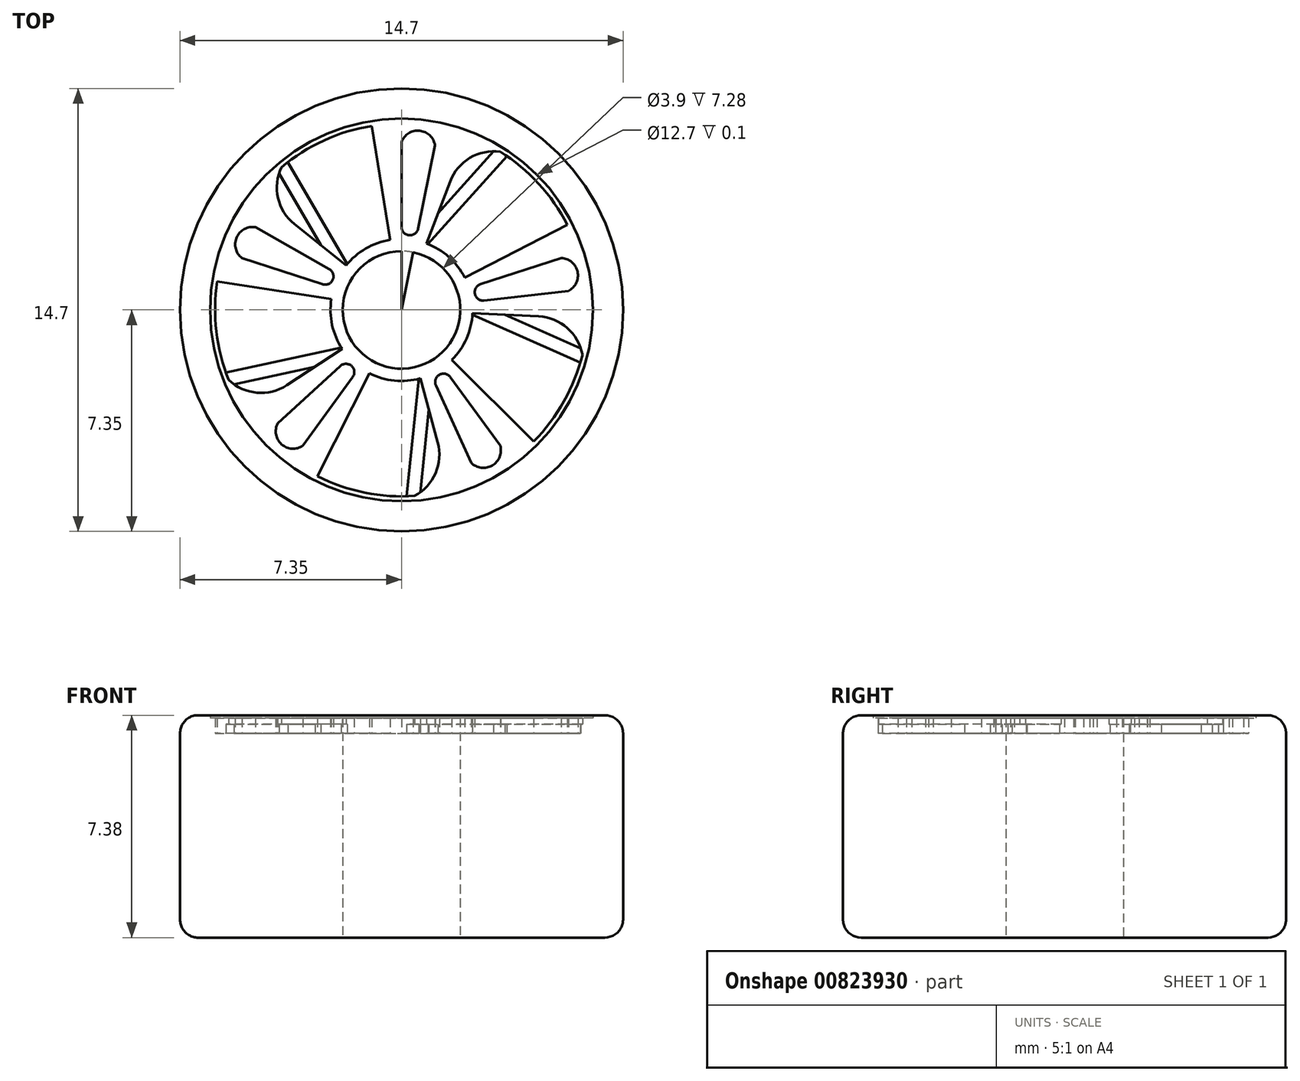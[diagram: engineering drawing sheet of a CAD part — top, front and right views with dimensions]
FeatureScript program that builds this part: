
annotation { "Feature Type Name" : "Feature", "Feature Type Description" : "" }
export const myFeature = defineFeature(function(context is Context, id is Id, definition is map)
    precondition{}
    {
        {
            var Q0;
            Q0=qCreatedBy(makeId("Front.planeOp"),FACE);
            var sketch = newSketch(context, id + "F0", { "sketchPlane" : qUnion([Q0])});
            skLineSegment(sketch, "E0.bottom", {"start": v(0, 0) * mm, "end": v(7.35, 0) * mm});
            skLineSegment(sketch, "E0.top", {"start": v(0, 7.38) * mm, "end": v(7.35, 7.38) * mm});
            skLineSegment(sketch, "E0.left", {"start": v(0, 0) * mm, "end": v(0, 7.38) * mm});
            skLineSegment(sketch, "E0.right", {"start": v(7.35, 0) * mm, "end": v(7.35, 7.38) * mm});
            skLineSegment(sketch, "E1.bottom", {"start": v(0, 7.38) * mm, "end": v(1.95, 7.38) * mm});
            skLineSegment(sketch, "E1.top", {"start": v(0, 0) * mm, "end": v(1.95, 0) * mm});
            skLineSegment(sketch, "E1.left", {"start": v(0, 7.38) * mm, "end": v(0, 0) * mm});
            skLineSegment(sketch, "E1.right", {"start": v(1.95, 7.38) * mm, "end": v(1.95, 0) * mm});
            skLineSegment(sketch, "E2.bottom", {"start": v(0, 7.38) * mm, "end": v(6.75, 7.38) * mm});
            skLineSegment(sketch, "E2.top", {"start": v(0, 0) * mm, "end": v(6.75, 0) * mm});
            skLineSegment(sketch, "E2.right", {"start": v(6.75, 7.38) * mm, "end": v(6.75, 0) * mm});
            skLineSegment(sketch, "E3.top", {"start": v(0, 6.78) * mm, "end": v(7.35, 6.78) * mm});
            skLineSegment(sketch, "E3.left", {"start": v(0, 0) * mm, "end": v(0, 6.78) * mm});
            skLineSegment(sketch, "E3.right", {"start": v(7.35, 0) * mm, "end": v(7.35, 6.78) * mm});
            skLineSegment(sketch, "E4.top", {"start": v(0, 0.6) * mm, "end": v(7.35, 0.6) * mm});
            skLineSegment(sketch, "E4.left", {"start": v(0, 7.38) * mm, "end": v(0, 0.6) * mm});
            skLineSegment(sketch, "E4.right", {"start": v(7.35, 7.38) * mm, "end": v(7.35, 0.6) * mm});
            skLineSegment(sketch, "E5.bottom", {"start": v(0, 7.38) * mm, "end": v(6.35, 7.38) * mm});
            skLineSegment(sketch, "E5.top", {"start": v(0, 0) * mm, "end": v(6.35, 0) * mm});
            skLineSegment(sketch, "E5.right", {"start": v(6.35, 7.38) * mm, "end": v(6.35, 0) * mm});
            skArc(sketch, "E6", {"start": v(7.35, 6.78) * mm, "mid": v(7.17, 7.2) * mm, "end": v(6.75, 7.38) * mm});
            skArc(sketch, "E7", {"start": v(6.75, 0) * mm, "mid": v(7.17, 0.18) * mm, "end": v(7.35, 0.6) * mm});
            skSolve(sketch);
        }
        {
            var Q0;
            {var subQ0=sQuery(id+"F0.wireOp",EDGE,"E3.top");var subQ1=sQuery(id+"F0.wireOp",EDGE,"E1.right");var subQ2=makeQuery(id+"F0.imprint","INTERSECT",VERTEX,{"derivedFrom":[subQ1,subQ0]});Q0=makeQuery(id+"F0.imprint","IMPRINT",FACE,{"disambiguationData":[TD([[makeQuery(id+"F0.imprint","IMPRINT",EDGE,{"disambiguationData":[TD([[subQ2,-1.0]])],"derivedFrom":subQ1}),1.0]])]});}
            var Q1;
            {var subQ0=sQuery(id+"F0.wireOp",EDGE,"E3.top");var subQ1=sQuery(id+"F0.wireOp",EDGE,"E2.right");var subQ2=makeQuery(id+"F0.imprint","INTERSECT",VERTEX,{"derivedFrom":[subQ1,subQ0]});Q1=makeQuery(id+"F0.imprint","IMPRINT",FACE,{"disambiguationData":[TD([[makeQuery(id+"F0.imprint","IMPRINT",EDGE,{"disambiguationData":[TD([[subQ2,-1.0]])],"derivedFrom":subQ1}),-1.0]])]});}
            var Q2;
            {var subQ0=sQuery(id+"F0.wireOp",EDGE,"E2.right");var subQ5=sQuery(id+"F0.wireOp",EDGE,"E3.top");var subQ6=makeQuery(id+"F0.imprint","INTERSECT",VERTEX,{"derivedFrom":[subQ0,subQ5]});Q2=makeQuery(id+"F0.imprint","IMPRINT",FACE,{"disambiguationData":[TD([[makeQuery(id+"F0.imprint","IMPRINT",EDGE,{"disambiguationData":[TD([[subQ6,1.0]])],"derivedFrom":subQ5}),1.0]])]});}
            var Q3;
            {var subQ0=sQuery(id+"F0.wireOp",EDGE,"E6");Q3=makeQuery(id+"F0.imprint","IMPRINT",FACE,{"disambiguationData":[TD([[makeQuery(id+"F0.imprint","IMPRINT",EDGE,{"derivedFrom":subQ0}),1.0]])]});}
            var Q4;
            {var subQ3=sQuery(id+"F0.wireOp",EDGE,"E3.top");var subQ5=sQuery(id+"F0.wireOp",EDGE,"E2.right");var subQ7=makeQuery(id+"F0.imprint","INTERSECT",VERTEX,{"derivedFrom":[subQ5,subQ3]});Q4=makeQuery(id+"F0.imprint","IMPRINT",FACE,{"disambiguationData":[TD([[makeQuery(id+"F0.imprint","IMPRINT",EDGE,{"disambiguationData":[TD([[subQ7,-1.0]])],"derivedFrom":subQ5}),1.0]])]});}
            var Q5;
            {var subQ0=sQuery(id+"F0.wireOp",EDGE,"E7");Q5=makeQuery(id+"F0.imprint","IMPRINT",FACE,{"disambiguationData":[TD([[makeQuery(id+"F0.imprint","IMPRINT",EDGE,{"derivedFrom":subQ0}),1.0]])]});}
            var Q6;
            {var subQ0=sQuery(id+"F0.wireOp",EDGE,"E2.right");var subQ5=sQuery(id+"F0.wireOp",EDGE,"E4.top");var subQ6=makeQuery(id+"F0.imprint","INTERSECT",VERTEX,{"derivedFrom":[subQ0,subQ5]});Q6=makeQuery(id+"F0.imprint","IMPRINT",FACE,{"disambiguationData":[TD([[makeQuery(id+"F0.imprint","IMPRINT",EDGE,{"disambiguationData":[TD([[subQ6,1.0]])],"derivedFrom":subQ5}),-1.0]])]});}
            var Q7;
            {var subQ0=sQuery(id+"F0.wireOp",EDGE,"E1.right");var subQ1=sQuery(id+"F0.wireOp",EDGE,"E0.bottom");var subQ2=makeQuery(id+"F0.imprint","INTERSECT",VERTEX,{"derivedFrom":[subQ1,subQ0]});Q7=makeQuery(id+"F0.imprint","IMPRINT",FACE,{"disambiguationData":[TD([[makeQuery(id+"F0.imprint","IMPRINT",EDGE,{"disambiguationData":[TD([[subQ2,-1.0]])],"derivedFrom":subQ1}),1.0]])]});}
            var Q8;
            Q8=sQuery(id+"F0.wireOp",EDGE,"E3.left");
            revolve(context, id + "F1", {"surfaceOperationType" : NewSurfaceOperationType.NEW, "entities" : qUnion([Q0, Q1, Q2, Q3, Q4, Q5, Q6, Q7]), "axis" : qUnion([Q8]), "revolveType" : RevolveType.FULL});
        }
        {
            var Q0;
            Q0=makeQuery(id+"F1.opRevolve","SWEPT_FACE",FACE,{"disambiguationData":[OSD([sQuery(id+"F0.wireOp",EDGE,"E3.top")])]});
            var sketch = newSketch(context, id + "F2", { "sketchPlane" : qUnion([Q0])});
            skLineSegment(sketch, "E8", {"start": v(0, 0) * mm, "end": v(2.25, 5.94) * mm});
            skArc(sketch, "E9", {"start": v(4.22, 4.75) * mm, "mid": v(2.78, 5.24) * mm, "end": v(1.61, 4.26) * mm});
            skLineSegment(sketch, "E10", {"start": v(0.79, 2.08) * mm, "end": v(3.56, 5.18) * mm});
            skLineSegment(sketch, "E11", {"start": v(3.05, 5.26) * mm, "end": v(1.21, 3.21) * mm});
            skCircle(sketch, "E12", {"center": v(0, 0) * mm, "radius": 2.36 * mm});
            skLineSegment(sketch, "E13", {"start": v(0, 0) * mm, "end": v(-1.02, 6.27) * mm});
            skLineSegment(sketch, "E14", {"start": v(0, 6.35) * mm, "end": v(0, 0) * mm});
            skLineSegment(sketch, "E15", {"start": v(1.27, 6.22) * mm, "end": v(0, 0) * mm});
            skCircle(sketch, "E16", {"center": v(0, 0) * mm, "radius": 6.19 * mm});
            skLineSegment(sketch, "E17", {"start": v(-0.99, 6.1) * mm, "end": v(2.19, 5.79) * mm});
            skLineSegment(sketch, "E18", {"start": v(0, 5.57) * mm, "end": v(1.11, 5.46) * mm});
            skLineSegment(sketch, "E19", {"start": v(-0.99, 6.1) * mm, "end": v(0.6, 5.95) * mm});
            skArc(sketch, "E20", {"start": v(1.11, 5.46) * mm, "mid": v(0.6, 5.95) * mm, "end": v(0, 5.57) * mm});
            skLineSegment(sketch, "E21", {"start": v(0, 2.75) * mm, "end": v(0.55, 2.7) * mm});
            skArc(sketch, "E22", {"start": v(0, 2.75) * mm, "mid": v(0.25, 2.48) * mm, "end": v(0.55, 2.7) * mm});
            skLineSegment(sketch, "E23.1.0", {"start": v(0, 0) * mm, "end": v(-6.28, 0.97) * mm});
            skLineSegment(sketch, "E23.1.1", {"start": v(-6.04, 1.96) * mm, "end": v(0, 0) * mm});
            skArc(sketch, "E23.1.2", {"start": v(-2.62, 0.85) * mm, "mid": v(-2.28, 1) * mm, "end": v(-2.4, 1.36) * mm});
            skArc(sketch, "E23.1.3", {"start": v(-4.85, 2.74) * mm, "mid": v(-5.47, 2.4) * mm, "end": v(-5.3, 1.72) * mm});
            skLineSegment(sketch, "E23.1.4", {"start": v(-5.53, 3.13) * mm, "end": v(0, 0) * mm});
            skLineSegment(sketch, "E23.1.5", {"start": v(0, 0) * mm, "end": v(-4.96, 3.97) * mm});
            skLineSegment(sketch, "E23.1.6", {"start": v(-1.73, 1.39) * mm, "end": v(-3.83, 4.99) * mm});
            skLineSegment(sketch, "E23.1.7", {"start": v(-4.06, 4.53) * mm, "end": v(-2.68, 2.15) * mm});
            skArc(sketch, "E23.1.8", {"start": v(-3.2, 5.48) * mm, "mid": v(-4.12, 4.26) * mm, "end": v(-3.55, 2.85) * mm});
            skLineSegment(sketch, "E23.2.0", {"start": v(0, 0) * mm, "end": v(-2.86, -5.67) * mm});
            skLineSegment(sketch, "E23.2.1", {"start": v(-3.73, -5.14) * mm, "end": v(0, 0) * mm});
            skArc(sketch, "E23.2.2", {"start": v(-1.62, -2.23) * mm, "mid": v(-1.66, -1.86) * mm, "end": v(-2.03, -1.86) * mm});
            skArc(sketch, "E23.2.3", {"start": v(-4.1, -3.76) * mm, "mid": v(-3.98, -4.46) * mm, "end": v(-3.27, -4.5) * mm});
            skLineSegment(sketch, "E23.2.4", {"start": v(-4.68, -4.29) * mm, "end": v(0, 0) * mm});
            skLineSegment(sketch, "E23.2.5", {"start": v(0, 0) * mm, "end": v(-5.3, -3.49) * mm});
            skLineSegment(sketch, "E23.2.6", {"start": v(-1.86, -1.22) * mm, "end": v(-5.93, -2.1) * mm});
            skLineSegment(sketch, "E23.2.7", {"start": v(-5.56, -2.47) * mm, "end": v(-2.87, -1.89) * mm});
            skArc(sketch, "E23.2.8", {"start": v(-6.2, -1.36) * mm, "mid": v(-5.33, -2.6) * mm, "end": v(-3.8, -2.5) * mm});
            skLineSegment(sketch, "E24.2.3.0", {"start": v(0, 0) * mm, "end": v(4.5, -4.47) * mm});
            skLineSegment(sketch, "E24.3.3.0", {"start": v(3.73, -5.14) * mm, "end": v(0, 0) * mm});
            skArc(sketch, "E24.6.3.0", {"start": v(1.62, -2.23) * mm, "mid": v(1.25, -2.15) * mm, "end": v(1.14, -2.5) * mm});
            skArc(sketch, "E24.10.3.0", {"start": v(2.31, -5.07) * mm, "mid": v(3.01, -5.16) * mm, "end": v(3.27, -4.5) * mm});
            skLineSegment(sketch, "E24.14.3.0", {"start": v(2.63, -5.78) * mm, "end": v(0, 0) * mm});
            skLineSegment(sketch, "E24.17.3.0", {"start": v(0, 0) * mm, "end": v(1.67, -6.13) * mm});
            skLineSegment(sketch, "E24.20.3.0", {"start": v(0.59, -2.14) * mm, "end": v(0.16, -6.29) * mm});
            skLineSegment(sketch, "E24.23.3.0", {"start": v(0.63, -6.05) * mm, "end": v(0.9, -3.31) * mm});
            skArc(sketch, "E24.26.3.0", {"start": v(-0.62, -6.32) * mm, "mid": v(0.83, -5.87) * mm, "end": v(1.2, -4.4) * mm});
            skLineSegment(sketch, "E24.2.4.0", {"start": v(0, 0) * mm, "end": v(5.65, 2.9) * mm});
            skLineSegment(sketch, "E24.3.4.0", {"start": v(6.04, 1.96) * mm, "end": v(0, 0) * mm});
            skArc(sketch, "E24.6.4.0", {"start": v(2.62, 0.85) * mm, "mid": v(2.43, 0.53) * mm, "end": v(2.74, 0.31) * mm});
            skArc(sketch, "E24.10.4.0", {"start": v(5.54, 0.63) * mm, "mid": v(5.84, 1.27) * mm, "end": v(5.3, 1.72) * mm});
            skLineSegment(sketch, "E24.14.4.0", {"start": v(6.3, 0.72) * mm, "end": v(0, 0) * mm});
            skLineSegment(sketch, "E24.17.4.0", {"start": v(0, 0) * mm, "end": v(6.34, -0.3) * mm});
            skLineSegment(sketch, "E24.20.4.0", {"start": v(2.22, -0.1) * mm, "end": v(6.03, -1.79) * mm});
            skLineSegment(sketch, "E24.23.4.0", {"start": v(5.95, -1.27) * mm, "end": v(3.43, -0.16) * mm});
            skArc(sketch, "E24.26.4.0", {"start": v(5.82, -2.55) * mm, "mid": v(5.84, -1.02) * mm, "end": v(4.55, -0.22) * mm});
            skSolve(sketch);
        }
        {
            var Q0;
            {var subQ0=sQuery(id+"F2.wireOp",EDGE,"E23.1.1");var subQ5=sQuery(id+"F2.wireOp",EDGE,"E12");var subQ9=makeQuery(id+"F2.imprint","INTERSECT",VERTEX,{"derivedFrom":[subQ5,subQ0]});Q0=makeQuery(id+"F2.imprint","IMPRINT",FACE,{"disambiguationData":[TD([[makeQuery(id+"F2.imprint","IMPRINT",EDGE,{"disambiguationData":[TD([[subQ9,-1.0]])],"derivedFrom":subQ5}),-1.0]])]});}
            var Q1;
            {var subQ5=sQuery(id+"F2.wireOp",EDGE,"E23.1.2");Q1=makeQuery(id+"F2.imprint","IMPRINT",FACE,{"disambiguationData":[TD([[makeQuery(id+"F2.imprint","IMPRINT",EDGE,{"derivedFrom":subQ5}),-1.0]])]});}
            var Q2;
            {var subQ5=sQuery(id+"F2.wireOp",EDGE,"E23.1.5");var subQ7=sQuery(id+"F2.wireOp",EDGE,"E12");var subQ8=makeQuery(id+"F2.imprint","INTERSECT",VERTEX,{"derivedFrom":[subQ7,subQ5]});Q2=makeQuery(id+"F2.imprint","IMPRINT",FACE,{"disambiguationData":[TD([[makeQuery(id+"F2.imprint","IMPRINT",EDGE,{"disambiguationData":[TD([[subQ8,-1.0]])],"derivedFrom":subQ7}),-1.0]])]});}
            var Q3;
            {var subQ0=sQuery(id+"F2.wireOp",EDGE,"E23.1.8");var subQ1=sQuery(id+"F2.wireOp",EDGE,"E16");var subQ2=makeQuery(id+"F2.imprint","INTERSECT",VERTEX,{"derivedFrom":[subQ1,subQ0]});Q3=makeQuery(id+"F2.imprint","IMPRINT",FACE,{"disambiguationData":[TD([[makeQuery(id+"F2.imprint","IMPRINT",EDGE,{"disambiguationData":[TD([[subQ2,-1.0]])],"derivedFrom":subQ1}),1.0]])]});}
            var Q4;
            {var subQ5=sQuery(id+"F2.wireOp",EDGE,"E22");Q4=makeQuery(id+"F2.imprint","IMPRINT",FACE,{"disambiguationData":[TD([[makeQuery(id+"F2.imprint","IMPRINT",EDGE,{"derivedFrom":subQ5}),-1.0]])]});}
            var Q5;
            {var subQ1=sQuery(id+"F2.wireOp",EDGE,"E8");var subQ8=makeQuery(id+"F2.imprint","INTERSECT",VERTEX,{"derivedFrom":[subQ1,sQuery(id+"F2.wireOp",EDGE,"E11")]});Q5=makeQuery(id+"F2.imprint","IMPRINT",FACE,{"disambiguationData":[TD([[makeQuery(id+"F2.imprint","IMPRINT",EDGE,{"disambiguationData":[TD([[subQ8,1.0]])],"derivedFrom":subQ1}),1.0]])]});}
            var Q6;
            {var subQ0=sQuery(id+"F2.wireOp",EDGE,"E14");var subQ7=sQuery(id+"F2.wireOp",EDGE,"E12");var subQ9=makeQuery(id+"F2.imprint","INTERSECT",VERTEX,{"derivedFrom":[subQ7,subQ0]});Q6=makeQuery(id+"F2.imprint","IMPRINT",FACE,{"disambiguationData":[TD([[makeQuery(id+"F2.imprint","IMPRINT",EDGE,{"disambiguationData":[TD([[subQ9,-1.0]])],"derivedFrom":subQ7}),-1.0]])]});}
            var Q7;
            {var subQ1=sQuery(id+"F2.wireOp",EDGE,"E14");var subQ3=sQuery(id+"F2.wireOp",EDGE,"E19");var subQ4=makeQuery(id+"F2.imprint","INTERSECT",VERTEX,{"derivedFrom":[subQ1,subQ3]});Q7=makeQuery(id+"F2.imprint","IMPRINT",FACE,{"disambiguationData":[TD([[makeQuery(id+"F2.imprint","IMPRINT",EDGE,{"disambiguationData":[TD([[subQ4,-1.0]])],"derivedFrom":subQ1}),1.0]])]});}
            var Q8;
            {var subQ5=sQuery(id+"F2.wireOp",EDGE,"E16");var subQ6=sQuery(id+"F2.wireOp",EDGE,"E14");var subQ7=makeQuery(id+"F2.imprint","INTERSECT",VERTEX,{"derivedFrom":[subQ6,subQ5]});Q8=makeQuery(id+"F2.imprint","IMPRINT",FACE,{"disambiguationData":[TD([[makeQuery(id+"F2.imprint","IMPRINT",EDGE,{"disambiguationData":[TD([[subQ7,-1.0]])],"derivedFrom":subQ6}),1.0]])]});}
            var Q9;
            {var subQ0=sQuery(id+"F2.wireOp",EDGE,"E16");var subQ1=sQuery(id+"F2.wireOp",EDGE,"E14");var subQ2=makeQuery(id+"F2.imprint","INTERSECT",VERTEX,{"derivedFrom":[subQ1,subQ0]});Q9=makeQuery(id+"F2.imprint","IMPRINT",FACE,{"disambiguationData":[TD([[makeQuery(id+"F2.imprint","IMPRINT",EDGE,{"disambiguationData":[TD([[subQ2,-1.0]])],"derivedFrom":subQ1}),-1.0]])]});}
            var Q10;
            {var subQ0=sQuery(id+"F2.wireOp",EDGE,"E16");var subQ1=sQuery(id+"F2.wireOp",EDGE,"E15");var subQ2=makeQuery(id+"F2.imprint","INTERSECT",VERTEX,{"derivedFrom":[subQ1,subQ0]});Q10=makeQuery(id+"F2.imprint","IMPRINT",FACE,{"disambiguationData":[TD([[makeQuery(id+"F2.imprint","IMPRINT",EDGE,{"disambiguationData":[TD([[subQ2,-1.0]])],"derivedFrom":subQ1}),1.0]])]});}
            var Q11;
            {var subQ1=sQuery(id+"F2.wireOp",EDGE,"E15");var subQ3=sQuery(id+"F2.wireOp",EDGE,"E17");var subQ4=makeQuery(id+"F2.imprint","INTERSECT",VERTEX,{"derivedFrom":[subQ1,subQ3]});Q11=makeQuery(id+"F2.imprint","IMPRINT",FACE,{"disambiguationData":[TD([[makeQuery(id+"F2.imprint","IMPRINT",EDGE,{"disambiguationData":[TD([[subQ4,-1.0]])],"derivedFrom":subQ1}),-1.0]])]});}
            var Q12;
            {var subQ0=sQuery(id+"F2.wireOp",EDGE,"E9");var subQ5=makeQuery(id+"F2.imprint","INTERSECT",VERTEX,{"derivedFrom":[subQ0,sQuery(id+"F2.wireOp",EDGE,"E11")]});Q12=makeQuery(id+"F2.imprint","IMPRINT",FACE,{"disambiguationData":[TD([[makeQuery(id+"F2.imprint","IMPRINT",EDGE,{"disambiguationData":[TD([[subQ5,1.0]])],"derivedFrom":subQ0}),-1.0]])]});}
            var Q13;
            {var subQ5=sQuery(id+"F2.wireOp",EDGE,"E24.10.4.0");Q13=makeQuery(id+"F2.imprint","IMPRINT",FACE,{"disambiguationData":[TD([[makeQuery(id+"F2.imprint","IMPRINT",EDGE,{"derivedFrom":subQ5}),-1.0]])]});}
            var Q14;
            {var subQ0=sQuery(id+"F2.wireOp",EDGE,"E24.14.4.0");var subQ7=sQuery(id+"F2.wireOp",EDGE,"E12");var subQ8=makeQuery(id+"F2.imprint","INTERSECT",VERTEX,{"derivedFrom":[subQ7,subQ0]});Q14=makeQuery(id+"F2.imprint","IMPRINT",FACE,{"disambiguationData":[TD([[makeQuery(id+"F2.imprint","IMPRINT",EDGE,{"disambiguationData":[TD([[subQ8,1.0]])],"derivedFrom":subQ7}),-1.0]])]});}
            var Q15;
            {var subQ0=sQuery(id+"F2.wireOp",EDGE,"E24.26.4.0");var subQ1=sQuery(id+"F2.wireOp",EDGE,"E16");var subQ2=makeQuery(id+"F2.imprint","INTERSECT",VERTEX,{"derivedFrom":[subQ1,subQ0]});Q15=makeQuery(id+"F2.imprint","IMPRINT",FACE,{"disambiguationData":[TD([[makeQuery(id+"F2.imprint","IMPRINT",EDGE,{"disambiguationData":[TD([[subQ2,-1.0]])],"derivedFrom":subQ1}),1.0]])]});}
            var Q16;
            {var subQ0=sQuery(id+"F2.wireOp",EDGE,"E24.3.3.0");var subQ5=sQuery(id+"F2.wireOp",EDGE,"E12");var subQ9=makeQuery(id+"F2.imprint","INTERSECT",VERTEX,{"derivedFrom":[subQ5,subQ0]});Q16=makeQuery(id+"F2.imprint","IMPRINT",FACE,{"disambiguationData":[TD([[makeQuery(id+"F2.imprint","IMPRINT",EDGE,{"disambiguationData":[TD([[subQ9,-1.0]])],"derivedFrom":subQ5}),-1.0]])]});}
            var Q17;
            {var subQ5=sQuery(id+"F2.wireOp",EDGE,"E24.10.3.0");Q17=makeQuery(id+"F2.imprint","IMPRINT",FACE,{"disambiguationData":[TD([[makeQuery(id+"F2.imprint","IMPRINT",EDGE,{"derivedFrom":subQ5}),-1.0]])]});}
            var Q18;
            {var subQ5=sQuery(id+"F2.wireOp",EDGE,"E24.6.4.0");Q18=makeQuery(id+"F2.imprint","IMPRINT",FACE,{"disambiguationData":[TD([[makeQuery(id+"F2.imprint","IMPRINT",EDGE,{"derivedFrom":subQ5}),-1.0]])]});}
            var Q19;
            {var subQ5=sQuery(id+"F2.wireOp",EDGE,"E24.6.3.0");Q19=makeQuery(id+"F2.imprint","IMPRINT",FACE,{"disambiguationData":[TD([[makeQuery(id+"F2.imprint","IMPRINT",EDGE,{"derivedFrom":subQ5}),-1.0]])]});}
            var Q20;
            {var subQ4=sQuery(id+"F2.wireOp",EDGE,"E24.17.3.0");var subQ7=sQuery(id+"F2.wireOp",EDGE,"E12");var subQ9=makeQuery(id+"F2.imprint","INTERSECT",VERTEX,{"derivedFrom":[subQ7,subQ4]});Q20=makeQuery(id+"F2.imprint","IMPRINT",FACE,{"disambiguationData":[TD([[makeQuery(id+"F2.imprint","IMPRINT",EDGE,{"disambiguationData":[TD([[subQ9,-1.0]])],"derivedFrom":subQ7}),-1.0]])]});}
            var Q21;
            {var subQ0=sQuery(id+"F2.wireOp",EDGE,"E24.26.3.0");var subQ1=sQuery(id+"F2.wireOp",EDGE,"E16");var subQ2=makeQuery(id+"F2.imprint","INTERSECT",VERTEX,{"derivedFrom":[subQ1,subQ0]});Q21=makeQuery(id+"F2.imprint","IMPRINT",FACE,{"disambiguationData":[TD([[makeQuery(id+"F2.imprint","IMPRINT",EDGE,{"disambiguationData":[TD([[subQ2,-1.0]])],"derivedFrom":subQ1}),1.0]])]});}
            var Q22;
            {var subQ5=sQuery(id+"F2.wireOp",EDGE,"E23.2.2");Q22=makeQuery(id+"F2.imprint","IMPRINT",FACE,{"disambiguationData":[TD([[makeQuery(id+"F2.imprint","IMPRINT",EDGE,{"derivedFrom":subQ5}),-1.0]])]});}
            var Q23;
            {var subQ5=sQuery(id+"F2.wireOp",EDGE,"E23.2.3");Q23=makeQuery(id+"F2.imprint","IMPRINT",FACE,{"disambiguationData":[TD([[makeQuery(id+"F2.imprint","IMPRINT",EDGE,{"derivedFrom":subQ5}),-1.0]])]});}
            var Q24;
            {var subQ1=sQuery(id+"F2.wireOp",EDGE,"E12");var subQ5=sQuery(id+"F2.wireOp",EDGE,"E23.2.1");var subQ8=makeQuery(id+"F2.imprint","INTERSECT",VERTEX,{"derivedFrom":[subQ1,subQ5]});Q24=makeQuery(id+"F2.imprint","IMPRINT",FACE,{"disambiguationData":[TD([[makeQuery(id+"F2.imprint","IMPRINT",EDGE,{"disambiguationData":[TD([[subQ8,-1.0]])],"derivedFrom":subQ1}),-1.0]])]});}
            var Q25;
            {var subQ3=sQuery(id+"F2.wireOp",EDGE,"E23.2.5");var subQ8=sQuery(id+"F2.wireOp",EDGE,"E12");var subQ9=makeQuery(id+"F2.imprint","INTERSECT",VERTEX,{"derivedFrom":[subQ8,subQ3]});Q25=makeQuery(id+"F2.imprint","IMPRINT",FACE,{"disambiguationData":[TD([[makeQuery(id+"F2.imprint","IMPRINT",EDGE,{"disambiguationData":[TD([[subQ9,-1.0]])],"derivedFrom":subQ8}),-1.0]])]});}
            var Q26;
            {var subQ0=sQuery(id+"F2.wireOp",EDGE,"E23.2.8");var subQ1=sQuery(id+"F2.wireOp",EDGE,"E16");var subQ2=makeQuery(id+"F2.imprint","INTERSECT",VERTEX,{"derivedFrom":[subQ1,subQ0]});Q26=makeQuery(id+"F2.imprint","IMPRINT",FACE,{"disambiguationData":[TD([[makeQuery(id+"F2.imprint","IMPRINT",EDGE,{"disambiguationData":[TD([[subQ2,-1.0]])],"derivedFrom":subQ1}),1.0]])]});}
            var Q27;
            {var subQ0=sQuery(id+"F2.wireOp",EDGE,"E23.2.1");var subQ1=sQuery(id+"F2.wireOp",EDGE,"E12");var subQ2=makeQuery(id+"F2.imprint","INTERSECT",VERTEX,{"derivedFrom":[subQ1,subQ0]});Q27=makeQuery(id+"F2.imprint","IMPRINT",FACE,{"disambiguationData":[TD([[makeQuery(id+"F2.imprint","IMPRINT",EDGE,{"disambiguationData":[TD([[subQ2,-1.0]])],"derivedFrom":subQ1}),1.0]])]});}
            var Q28;
            {var subQ0=sQuery(id+"F2.wireOp",EDGE,"E23.2.4");var subQ1=sQuery(id+"F2.wireOp",EDGE,"E12");var subQ2=makeQuery(id+"F2.imprint","INTERSECT",VERTEX,{"derivedFrom":[subQ1,subQ0]});Q28=makeQuery(id+"F2.imprint","IMPRINT",FACE,{"disambiguationData":[TD([[makeQuery(id+"F2.imprint","IMPRINT",EDGE,{"disambiguationData":[TD([[subQ2,-1.0]])],"derivedFrom":subQ1}),1.0]])]});}
            var Q29;
            {var subQ0=sQuery(id+"F2.wireOp",EDGE,"E23.2.5");var subQ2=sQuery(id+"F2.wireOp",EDGE,"E12");var subQ3=makeQuery(id+"F2.imprint","INTERSECT",VERTEX,{"derivedFrom":[subQ2,subQ0]});Q29=makeQuery(id+"F2.imprint","IMPRINT",FACE,{"disambiguationData":[TD([[makeQuery(id+"F2.imprint","IMPRINT",EDGE,{"disambiguationData":[TD([[subQ3,-1.0]])],"derivedFrom":subQ2}),1.0]])]});}
            var Q30;
            {var subQ3=sQuery(id+"F2.wireOp",EDGE,"E12");var subQ7=sQuery(id+"F2.wireOp",EDGE,"E23.1.0");var subQ8=makeQuery(id+"F2.imprint","INTERSECT",VERTEX,{"derivedFrom":[subQ3,subQ7]});Q30=makeQuery(id+"F2.imprint","IMPRINT",FACE,{"disambiguationData":[TD([[makeQuery(id+"F2.imprint","IMPRINT",EDGE,{"disambiguationData":[TD([[subQ8,-1.0]])],"derivedFrom":subQ3}),1.0]])]});}
            var Q31;
            {var subQ0=sQuery(id+"F2.wireOp",EDGE,"E23.1.1");var subQ1=sQuery(id+"F2.wireOp",EDGE,"E12");var subQ2=makeQuery(id+"F2.imprint","INTERSECT",VERTEX,{"derivedFrom":[subQ1,subQ0]});Q31=makeQuery(id+"F2.imprint","IMPRINT",FACE,{"disambiguationData":[TD([[makeQuery(id+"F2.imprint","IMPRINT",EDGE,{"disambiguationData":[TD([[subQ2,-1.0]])],"derivedFrom":subQ1}),1.0]])]});}
            var Q32;
            {var subQ0=sQuery(id+"F2.wireOp",EDGE,"E23.1.4");var subQ1=sQuery(id+"F2.wireOp",EDGE,"E12");var subQ2=makeQuery(id+"F2.imprint","INTERSECT",VERTEX,{"derivedFrom":[subQ1,subQ0]});Q32=makeQuery(id+"F2.imprint","IMPRINT",FACE,{"disambiguationData":[TD([[makeQuery(id+"F2.imprint","IMPRINT",EDGE,{"disambiguationData":[TD([[subQ2,-1.0]])],"derivedFrom":subQ1}),1.0]])]});}
            var Q33;
            {var subQ5=sQuery(id+"F2.wireOp",EDGE,"E13");var subQ6=sQuery(id+"F2.wireOp",EDGE,"E12");var subQ7=makeQuery(id+"F2.imprint","INTERSECT",VERTEX,{"derivedFrom":[subQ6,subQ5]});Q33=makeQuery(id+"F2.imprint","IMPRINT",FACE,{"disambiguationData":[TD([[makeQuery(id+"F2.imprint","IMPRINT",EDGE,{"disambiguationData":[TD([[subQ7,-1.0]])],"derivedFrom":subQ6}),1.0]])]});}
            var Q34;
            {var subQ0=sQuery(id+"F2.wireOp",EDGE,"E14");var subQ1=sQuery(id+"F2.wireOp",EDGE,"E12");var subQ2=makeQuery(id+"F2.imprint","INTERSECT",VERTEX,{"derivedFrom":[subQ1,subQ0]});Q34=makeQuery(id+"F2.imprint","IMPRINT",FACE,{"disambiguationData":[TD([[makeQuery(id+"F2.imprint","IMPRINT",EDGE,{"disambiguationData":[TD([[subQ2,-1.0]])],"derivedFrom":subQ1}),1.0]])]});}
            var Q35;
            {var subQ0=sQuery(id+"F2.wireOp",EDGE,"E15");var subQ1=sQuery(id+"F2.wireOp",EDGE,"E12");var subQ2=makeQuery(id+"F2.imprint","INTERSECT",VERTEX,{"derivedFrom":[subQ1,subQ0]});Q35=makeQuery(id+"F2.imprint","IMPRINT",FACE,{"disambiguationData":[TD([[makeQuery(id+"F2.imprint","IMPRINT",EDGE,{"disambiguationData":[TD([[subQ2,-1.0]])],"derivedFrom":subQ1}),1.0]])]});}
            var Q36;
            {var subQ1=sQuery(id+"F2.wireOp",EDGE,"E8");var subQ7=makeQuery(id+"F2.imprint","INTERSECT",VERTEX,{"derivedFrom":[subQ1,sQuery(id+"F2.wireOp",EDGE,"E10")]});Q36=makeQuery(id+"F2.imprint","IMPRINT",FACE,{"disambiguationData":[TD([[makeQuery(id+"F2.imprint","IMPRINT",EDGE,{"disambiguationData":[TD([[subQ7,-1.0]])],"derivedFrom":subQ1}),1.0]])]});}
            var Q37;
            {var subQ1=sQuery(id+"F2.wireOp",EDGE,"E10");var subQ5=sQuery(id+"F2.wireOp",EDGE,"E8");var subQ6=makeQuery(id+"F2.imprint","INTERSECT",VERTEX,{"derivedFrom":[subQ5,subQ1]});Q37=makeQuery(id+"F2.imprint","IMPRINT",FACE,{"disambiguationData":[TD([[makeQuery(id+"F2.imprint","IMPRINT",EDGE,{"disambiguationData":[TD([[subQ6,-1.0]])],"derivedFrom":subQ1}),-1.0]])]});}
            var Q38;
            {var subQ0=sQuery(id+"F2.wireOp",EDGE,"E24.3.4.0");var subQ1=sQuery(id+"F2.wireOp",EDGE,"E12");var subQ2=makeQuery(id+"F2.imprint","INTERSECT",VERTEX,{"derivedFrom":[subQ1,subQ0]});Q38=makeQuery(id+"F2.imprint","IMPRINT",FACE,{"disambiguationData":[TD([[makeQuery(id+"F2.imprint","IMPRINT",EDGE,{"disambiguationData":[TD([[subQ2,-1.0]])],"derivedFrom":subQ1}),1.0]])]});}
            var Q39;
            {var subQ0=sQuery(id+"F2.wireOp",EDGE,"E24.3.4.0");var subQ1=sQuery(id+"F2.wireOp",EDGE,"E12");var subQ2=makeQuery(id+"F2.imprint","INTERSECT",VERTEX,{"derivedFrom":[subQ1,subQ0]});Q39=makeQuery(id+"F2.imprint","IMPRINT",FACE,{"disambiguationData":[TD([[makeQuery(id+"F2.imprint","IMPRINT",EDGE,{"disambiguationData":[TD([[subQ2,1.0]])],"derivedFrom":subQ1}),1.0]])]});}
            var Q40;
            {var subQ4=sQuery(id+"F2.wireOp",EDGE,"E24.14.4.0");var subQ5=sQuery(id+"F2.wireOp",EDGE,"E12");var subQ6=makeQuery(id+"F2.imprint","INTERSECT",VERTEX,{"derivedFrom":[subQ5,subQ4]});Q40=makeQuery(id+"F2.imprint","IMPRINT",FACE,{"disambiguationData":[TD([[makeQuery(id+"F2.imprint","IMPRINT",EDGE,{"disambiguationData":[TD([[subQ6,1.0]])],"derivedFrom":subQ5}),1.0]])]});}
            var Q41;
            {var subQ3=sQuery(id+"F2.wireOp",EDGE,"E12");var subQ5=sQuery(id+"F2.wireOp",EDGE,"E24.2.3.0");var subQ6=makeQuery(id+"F2.imprint","INTERSECT",VERTEX,{"derivedFrom":[subQ3,subQ5]});Q41=makeQuery(id+"F2.imprint","IMPRINT",FACE,{"disambiguationData":[TD([[makeQuery(id+"F2.imprint","IMPRINT",EDGE,{"disambiguationData":[TD([[subQ6,-1.0]])],"derivedFrom":subQ3}),1.0]])]});}
            var Q42;
            {var subQ0=sQuery(id+"F2.wireOp",EDGE,"E24.3.3.0");var subQ1=sQuery(id+"F2.wireOp",EDGE,"E12");var subQ2=makeQuery(id+"F2.imprint","INTERSECT",VERTEX,{"derivedFrom":[subQ1,subQ0]});Q42=makeQuery(id+"F2.imprint","IMPRINT",FACE,{"disambiguationData":[TD([[makeQuery(id+"F2.imprint","IMPRINT",EDGE,{"disambiguationData":[TD([[subQ2,-1.0]])],"derivedFrom":subQ1}),1.0]])]});}
            var Q43;
            {var subQ0=sQuery(id+"F2.wireOp",EDGE,"E24.14.3.0");var subQ1=sQuery(id+"F2.wireOp",EDGE,"E12");var subQ2=makeQuery(id+"F2.imprint","INTERSECT",VERTEX,{"derivedFrom":[subQ1,subQ0]});Q43=makeQuery(id+"F2.imprint","IMPRINT",FACE,{"disambiguationData":[TD([[makeQuery(id+"F2.imprint","IMPRINT",EDGE,{"disambiguationData":[TD([[subQ2,-1.0]])],"derivedFrom":subQ1}),1.0]])]});}
            var Q44;
            {var subQ0=sQuery(id+"F2.wireOp",EDGE,"E24.17.3.0");var subQ2=sQuery(id+"F2.wireOp",EDGE,"E12");var subQ3=makeQuery(id+"F2.imprint","INTERSECT",VERTEX,{"derivedFrom":[subQ2,subQ0]});Q44=makeQuery(id+"F2.imprint","IMPRINT",FACE,{"disambiguationData":[TD([[makeQuery(id+"F2.imprint","IMPRINT",EDGE,{"disambiguationData":[TD([[subQ3,-1.0]])],"derivedFrom":subQ2}),1.0]])]});}
            var Q45;
            {var subQ3=sQuery(id+"F2.wireOp",EDGE,"E12");var subQ7=sQuery(id+"F2.wireOp",EDGE,"E23.2.0");var subQ8=makeQuery(id+"F2.imprint","INTERSECT",VERTEX,{"derivedFrom":[subQ3,subQ7]});Q45=makeQuery(id+"F2.imprint","IMPRINT",FACE,{"disambiguationData":[TD([[makeQuery(id+"F2.imprint","IMPRINT",EDGE,{"disambiguationData":[TD([[subQ8,-1.0]])],"derivedFrom":subQ3}),1.0]])]});}
            var Q46;
            {var subQ0=sQuery(id+"F2.wireOp",EDGE,"E23.1.5");var subQ2=sQuery(id+"F2.wireOp",EDGE,"E12");var subQ3=makeQuery(id+"F2.imprint","INTERSECT",VERTEX,{"derivedFrom":[subQ2,subQ0]});Q46=makeQuery(id+"F2.imprint","IMPRINT",FACE,{"disambiguationData":[TD([[makeQuery(id+"F2.imprint","IMPRINT",EDGE,{"disambiguationData":[TD([[subQ3,-1.0]])],"derivedFrom":subQ2}),1.0]])]});}
            var Q47;
            {var subQ0=sQuery(id+"F2.wireOp",EDGE,"E23.2.6");var subQ1=sQuery(id+"F2.wireOp",EDGE,"E12");var subQ2=makeQuery(id+"F2.imprint","INTERSECT",VERTEX,{"derivedFrom":[subQ1,subQ0]});Q47=makeQuery(id+"F2.imprint","IMPRINT",FACE,{"disambiguationData":[TD([[makeQuery(id+"F2.imprint","IMPRINT",EDGE,{"disambiguationData":[TD([[subQ2,-1.0]])],"derivedFrom":subQ1}),1.0]])]});}
            var Q48;
            {var subQ0=sQuery(id+"F2.wireOp",EDGE,"E23.1.6");var subQ1=sQuery(id+"F2.wireOp",EDGE,"E12");var subQ2=makeQuery(id+"F2.imprint","INTERSECT",VERTEX,{"derivedFrom":[subQ1,subQ0]});Q48=makeQuery(id+"F2.imprint","IMPRINT",FACE,{"disambiguationData":[TD([[makeQuery(id+"F2.imprint","IMPRINT",EDGE,{"disambiguationData":[TD([[subQ2,-1.0]])],"derivedFrom":subQ1}),1.0]])]});}
            var Q49;
            {var subQ0=sQuery(id+"F2.wireOp",EDGE,"E10");var subQ1=sQuery(id+"F2.wireOp",EDGE,"E8");var subQ2=makeQuery(id+"F2.imprint","INTERSECT",VERTEX,{"derivedFrom":[subQ1,subQ0]});Q49=makeQuery(id+"F2.imprint","IMPRINT",FACE,{"disambiguationData":[TD([[makeQuery(id+"F2.imprint","IMPRINT",EDGE,{"disambiguationData":[TD([[subQ2,-1.0]])],"derivedFrom":subQ1}),-1.0]])]});}
            var Q50;
            {var subQ0=sQuery(id+"F2.wireOp",EDGE,"E24.20.4.0");var subQ1=sQuery(id+"F2.wireOp",EDGE,"E12");var subQ2=makeQuery(id+"F2.imprint","INTERSECT",VERTEX,{"derivedFrom":[subQ1,subQ0]});Q50=makeQuery(id+"F2.imprint","IMPRINT",FACE,{"disambiguationData":[TD([[makeQuery(id+"F2.imprint","IMPRINT",EDGE,{"disambiguationData":[TD([[subQ2,-1.0]])],"derivedFrom":subQ1}),1.0]])]});}
            var Q51;
            {var subQ0=sQuery(id+"F2.wireOp",EDGE,"E24.20.3.0");var subQ1=sQuery(id+"F2.wireOp",EDGE,"E12");var subQ2=makeQuery(id+"F2.imprint","INTERSECT",VERTEX,{"derivedFrom":[subQ1,subQ0]});Q51=makeQuery(id+"F2.imprint","IMPRINT",FACE,{"disambiguationData":[TD([[makeQuery(id+"F2.imprint","IMPRINT",EDGE,{"disambiguationData":[TD([[subQ2,-1.0]])],"derivedFrom":subQ1}),1.0]])]});}
            var Q52;
            {var subQ0=sQuery(id+"F2.wireOp",EDGE,"E23.1.8");var subQ1=sQuery(id+"F2.wireOp",EDGE,"E23.1.6");var subQ2=makeQuery(id+"F2.imprint","INTERSECT",VERTEX,{"derivedFrom":[subQ1,subQ0]});Q52=makeQuery(id+"F2.imprint","IMPRINT",FACE,{"disambiguationData":[TD([[makeQuery(id+"F2.imprint","IMPRINT",EDGE,{"disambiguationData":[TD([[subQ2,1.0]])],"derivedFrom":subQ1}),-1.0]])]});}
            var Q53;
            {var subQ3=sQuery(id+"F2.wireOp",EDGE,"E16");var subQ5=sQuery(id+"F2.wireOp",EDGE,"E14");var subQ7=makeQuery(id+"F2.imprint","INTERSECT",VERTEX,{"derivedFrom":[subQ5,subQ3]});Q53=makeQuery(id+"F2.imprint","IMPRINT",FACE,{"disambiguationData":[TD([[makeQuery(id+"F2.imprint","IMPRINT",EDGE,{"disambiguationData":[TD([[subQ7,1.0]])],"derivedFrom":subQ5}),-1.0]])]});}
            var Q54;
            {var subQ0=sQuery(id+"F2.wireOp",EDGE,"E14");var subQ3=sQuery(id+"F2.wireOp",EDGE,"E16");var subQ4=makeQuery(id+"F2.imprint","INTERSECT",VERTEX,{"derivedFrom":[subQ0,subQ3]});Q54=makeQuery(id+"F2.imprint","IMPRINT",FACE,{"disambiguationData":[TD([[makeQuery(id+"F2.imprint","IMPRINT",EDGE,{"disambiguationData":[TD([[subQ4,1.0]])],"derivedFrom":subQ3}),-1.0]])]});}
            var Q55;
            {var subQ3=sQuery(id+"F2.wireOp",EDGE,"E16");var subQ5=sQuery(id+"F2.wireOp",EDGE,"E15");var subQ7=makeQuery(id+"F2.imprint","INTERSECT",VERTEX,{"derivedFrom":[subQ5,subQ3]});Q55=makeQuery(id+"F2.imprint","IMPRINT",FACE,{"disambiguationData":[TD([[makeQuery(id+"F2.imprint","IMPRINT",EDGE,{"disambiguationData":[TD([[subQ7,1.0]])],"derivedFrom":subQ5}),1.0]])]});}
            var Q56;
            {var subQ1=sQuery(id+"F2.wireOp",EDGE,"E10");var subQ5=sQuery(id+"F2.wireOp",EDGE,"E9");var subQ9=makeQuery(id+"F2.imprint","INTERSECT",VERTEX,{"derivedFrom":[subQ5,subQ1]});Q56=makeQuery(id+"F2.imprint","IMPRINT",FACE,{"disambiguationData":[TD([[makeQuery(id+"F2.imprint","IMPRINT",EDGE,{"disambiguationData":[TD([[subQ9,1.0]])],"derivedFrom":subQ1}),-1.0]])]});}
            var Q57;
            {var subQ0=sQuery(id+"F2.wireOp",EDGE,"E9");var subQ1=makeQuery(id+"F2.imprint","INTERSECT",VERTEX,{"derivedFrom":[subQ0,sQuery(id+"F2.wireOp",EDGE,"E10")]});Q57=makeQuery(id+"F2.imprint","IMPRINT",FACE,{"disambiguationData":[TD([[makeQuery(id+"F2.imprint","IMPRINT",EDGE,{"disambiguationData":[TD([[subQ1,-1.0]])],"derivedFrom":subQ0}),-1.0]])]});}
            var Q58;
            {var subQ0=sQuery(id+"F2.wireOp",EDGE,"E24.3.4.0");var subQ1=sQuery(id+"F2.wireOp",EDGE,"E16");var subQ2=makeQuery(id+"F2.imprint","INTERSECT",VERTEX,{"derivedFrom":[subQ1,subQ0]});Q58=makeQuery(id+"F2.imprint","IMPRINT",FACE,{"disambiguationData":[TD([[makeQuery(id+"F2.imprint","IMPRINT",EDGE,{"disambiguationData":[TD([[subQ2,1.0]])],"derivedFrom":subQ1}),-1.0]])]});}
            var Q59;
            {var subQ0=sQuery(id+"F2.wireOp",EDGE,"E24.14.4.0");var subQ1=sQuery(id+"F2.wireOp",EDGE,"E16");var subQ2=makeQuery(id+"F2.imprint","INTERSECT",VERTEX,{"derivedFrom":[subQ1,subQ0]});Q59=makeQuery(id+"F2.imprint","IMPRINT",FACE,{"disambiguationData":[TD([[makeQuery(id+"F2.imprint","IMPRINT",EDGE,{"disambiguationData":[TD([[subQ2,1.0]])],"derivedFrom":subQ1}),-1.0]])]});}
            var Q60;
            {var subQ0=sQuery(id+"F2.wireOp",EDGE,"E24.26.4.0");var subQ2=sQuery(id+"F2.wireOp",EDGE,"E16");var subQ3=makeQuery(id+"F2.imprint","INTERSECT",VERTEX,{"derivedFrom":[subQ2,subQ0]});Q60=makeQuery(id+"F2.imprint","IMPRINT",FACE,{"disambiguationData":[TD([[makeQuery(id+"F2.imprint","IMPRINT",EDGE,{"disambiguationData":[TD([[subQ3,-1.0]])],"derivedFrom":subQ2}),-1.0]])]});}
            var Q61;
            {var subQ3=sQuery(id+"F2.wireOp",EDGE,"E16");var subQ5=sQuery(id+"F2.wireOp",EDGE,"E24.2.3.0");var subQ8=makeQuery(id+"F2.imprint","INTERSECT",VERTEX,{"derivedFrom":[subQ3,subQ5]});Q61=makeQuery(id+"F2.imprint","IMPRINT",FACE,{"disambiguationData":[TD([[makeQuery(id+"F2.imprint","IMPRINT",EDGE,{"disambiguationData":[TD([[subQ8,-1.0]])],"derivedFrom":subQ3}),-1.0]])]});}
            var Q62;
            {var subQ0=sQuery(id+"F2.wireOp",EDGE,"E24.3.3.0");var subQ1=sQuery(id+"F2.wireOp",EDGE,"E16");var subQ2=makeQuery(id+"F2.imprint","INTERSECT",VERTEX,{"derivedFrom":[subQ1,subQ0]});Q62=makeQuery(id+"F2.imprint","IMPRINT",FACE,{"disambiguationData":[TD([[makeQuery(id+"F2.imprint","IMPRINT",EDGE,{"disambiguationData":[TD([[subQ2,-1.0]])],"derivedFrom":subQ1}),-1.0]])]});}
            var Q63;
            {var subQ0=sQuery(id+"F2.wireOp",EDGE,"E24.14.3.0");var subQ1=sQuery(id+"F2.wireOp",EDGE,"E16");var subQ2=makeQuery(id+"F2.imprint","INTERSECT",VERTEX,{"derivedFrom":[subQ1,subQ0]});Q63=makeQuery(id+"F2.imprint","IMPRINT",FACE,{"disambiguationData":[TD([[makeQuery(id+"F2.imprint","IMPRINT",EDGE,{"disambiguationData":[TD([[subQ2,-1.0]])],"derivedFrom":subQ1}),-1.0]])]});}
            var Q64;
            {var subQ0=sQuery(id+"F2.wireOp",EDGE,"E24.17.3.0");var subQ1=sQuery(id+"F2.wireOp",EDGE,"E16");var subQ2=makeQuery(id+"F2.imprint","INTERSECT",VERTEX,{"derivedFrom":[subQ1,subQ0]});Q64=makeQuery(id+"F2.imprint","IMPRINT",FACE,{"disambiguationData":[TD([[makeQuery(id+"F2.imprint","IMPRINT",EDGE,{"disambiguationData":[TD([[subQ2,-1.0]])],"derivedFrom":subQ1}),-1.0]])]});}
            var Q65;
            {var subQ0=sQuery(id+"F2.wireOp",EDGE,"E24.26.3.0");var subQ2=sQuery(id+"F2.wireOp",EDGE,"E16");var subQ3=makeQuery(id+"F2.imprint","INTERSECT",VERTEX,{"derivedFrom":[subQ2,subQ0]});Q65=makeQuery(id+"F2.imprint","IMPRINT",FACE,{"disambiguationData":[TD([[makeQuery(id+"F2.imprint","IMPRINT",EDGE,{"disambiguationData":[TD([[subQ3,-1.0]])],"derivedFrom":subQ2}),-1.0]])]});}
            var Q66;
            {var subQ6=sQuery(id+"F2.wireOp",EDGE,"E16");var subQ8=sQuery(id+"F2.wireOp",EDGE,"E23.2.0");var subQ10=makeQuery(id+"F2.imprint","INTERSECT",VERTEX,{"derivedFrom":[subQ6,subQ8]});Q66=makeQuery(id+"F2.imprint","IMPRINT",FACE,{"disambiguationData":[TD([[makeQuery(id+"F2.imprint","IMPRINT",EDGE,{"disambiguationData":[TD([[subQ10,-1.0]])],"derivedFrom":subQ6}),-1.0]])]});}
            var Q67;
            {var subQ0=sQuery(id+"F2.wireOp",EDGE,"E23.2.1");var subQ1=sQuery(id+"F2.wireOp",EDGE,"E16");var subQ2=makeQuery(id+"F2.imprint","INTERSECT",VERTEX,{"derivedFrom":[subQ1,subQ0]});Q67=makeQuery(id+"F2.imprint","IMPRINT",FACE,{"disambiguationData":[TD([[makeQuery(id+"F2.imprint","IMPRINT",EDGE,{"disambiguationData":[TD([[subQ2,-1.0]])],"derivedFrom":subQ1}),-1.0]])]});}
            var Q68;
            {var subQ0=sQuery(id+"F2.wireOp",EDGE,"E23.2.4");var subQ1=sQuery(id+"F2.wireOp",EDGE,"E16");var subQ2=makeQuery(id+"F2.imprint","INTERSECT",VERTEX,{"derivedFrom":[subQ1,subQ0]});Q68=makeQuery(id+"F2.imprint","IMPRINT",FACE,{"disambiguationData":[TD([[makeQuery(id+"F2.imprint","IMPRINT",EDGE,{"disambiguationData":[TD([[subQ2,-1.0]])],"derivedFrom":subQ1}),-1.0]])]});}
            var Q69;
            {var subQ0=sQuery(id+"F2.wireOp",EDGE,"E23.2.5");var subQ1=sQuery(id+"F2.wireOp",EDGE,"E16");var subQ2=makeQuery(id+"F2.imprint","INTERSECT",VERTEX,{"derivedFrom":[subQ1,subQ0]});Q69=makeQuery(id+"F2.imprint","IMPRINT",FACE,{"disambiguationData":[TD([[makeQuery(id+"F2.imprint","IMPRINT",EDGE,{"disambiguationData":[TD([[subQ2,-1.0]])],"derivedFrom":subQ1}),-1.0]])]});}
            var Q70;
            {var subQ0=sQuery(id+"F2.wireOp",EDGE,"E23.2.8");var subQ2=sQuery(id+"F2.wireOp",EDGE,"E16");var subQ3=makeQuery(id+"F2.imprint","INTERSECT",VERTEX,{"derivedFrom":[subQ2,subQ0]});Q70=makeQuery(id+"F2.imprint","IMPRINT",FACE,{"disambiguationData":[TD([[makeQuery(id+"F2.imprint","IMPRINT",EDGE,{"disambiguationData":[TD([[subQ3,-1.0]])],"derivedFrom":subQ2}),-1.0]])]});}
            var Q71;
            {var subQ6=sQuery(id+"F2.wireOp",EDGE,"E16");var subQ8=sQuery(id+"F2.wireOp",EDGE,"E23.1.0");var subQ10=makeQuery(id+"F2.imprint","INTERSECT",VERTEX,{"derivedFrom":[subQ6,subQ8]});Q71=makeQuery(id+"F2.imprint","IMPRINT",FACE,{"disambiguationData":[TD([[makeQuery(id+"F2.imprint","IMPRINT",EDGE,{"disambiguationData":[TD([[subQ10,-1.0]])],"derivedFrom":subQ6}),-1.0]])]});}
            var Q72;
            {var subQ0=sQuery(id+"F2.wireOp",EDGE,"E23.1.1");var subQ1=sQuery(id+"F2.wireOp",EDGE,"E16");var subQ2=makeQuery(id+"F2.imprint","INTERSECT",VERTEX,{"derivedFrom":[subQ1,subQ0]});Q72=makeQuery(id+"F2.imprint","IMPRINT",FACE,{"disambiguationData":[TD([[makeQuery(id+"F2.imprint","IMPRINT",EDGE,{"disambiguationData":[TD([[subQ2,-1.0]])],"derivedFrom":subQ1}),-1.0]])]});}
            var Q73;
            {var subQ0=sQuery(id+"F2.wireOp",EDGE,"E23.1.4");var subQ1=sQuery(id+"F2.wireOp",EDGE,"E16");var subQ2=makeQuery(id+"F2.imprint","INTERSECT",VERTEX,{"derivedFrom":[subQ1,subQ0]});Q73=makeQuery(id+"F2.imprint","IMPRINT",FACE,{"disambiguationData":[TD([[makeQuery(id+"F2.imprint","IMPRINT",EDGE,{"disambiguationData":[TD([[subQ2,-1.0]])],"derivedFrom":subQ1}),-1.0]])]});}
            var Q74;
            {var subQ0=sQuery(id+"F2.wireOp",EDGE,"E23.1.5");var subQ1=sQuery(id+"F2.wireOp",EDGE,"E16");var subQ2=makeQuery(id+"F2.imprint","INTERSECT",VERTEX,{"derivedFrom":[subQ1,subQ0]});Q74=makeQuery(id+"F2.imprint","IMPRINT",FACE,{"disambiguationData":[TD([[makeQuery(id+"F2.imprint","IMPRINT",EDGE,{"disambiguationData":[TD([[subQ2,-1.0]])],"derivedFrom":subQ1}),-1.0]])]});}
            var Q75;
            {var subQ0=sQuery(id+"F2.wireOp",EDGE,"E23.1.8");var subQ6=sQuery(id+"F2.wireOp",EDGE,"E16");var subQ8=makeQuery(id+"F2.imprint","INTERSECT",VERTEX,{"derivedFrom":[subQ6,subQ0]});Q75=makeQuery(id+"F2.imprint","IMPRINT",FACE,{"disambiguationData":[TD([[makeQuery(id+"F2.imprint","IMPRINT",EDGE,{"disambiguationData":[TD([[subQ8,-1.0]])],"derivedFrom":subQ6}),-1.0]])]});}
            var Q76;
            {var subQ0=sQuery(id+"F2.wireOp",EDGE,"E24.3.4.0");var subQ6=sQuery(id+"F2.wireOp",EDGE,"E12");var subQ8=makeQuery(id+"F2.imprint","INTERSECT",VERTEX,{"derivedFrom":[subQ6,subQ0]});Q76=makeQuery(id+"F2.imprint","IMPRINT",FACE,{"disambiguationData":[TD([[makeQuery(id+"F2.imprint","IMPRINT",EDGE,{"disambiguationData":[TD([[subQ8,-1.0]])],"derivedFrom":subQ6}),-1.0]])]});}
            var Q77;
            {var subQ0=sQuery(id+"F2.wireOp",EDGE,"E24.3.4.0");var subQ1=sQuery(id+"F2.wireOp",EDGE,"E16");var subQ2=makeQuery(id+"F2.imprint","INTERSECT",VERTEX,{"derivedFrom":[subQ1,subQ0]});Q77=makeQuery(id+"F2.imprint","IMPRINT",FACE,{"disambiguationData":[TD([[makeQuery(id+"F2.imprint","IMPRINT",EDGE,{"disambiguationData":[TD([[subQ2,-1.0]])],"derivedFrom":subQ1}),-1.0]])]});}
            var Q78;
            {var subQ5=sQuery(id+"F2.wireOp",EDGE,"E23.1.3");Q78=makeQuery(id+"F2.imprint","IMPRINT",FACE,{"disambiguationData":[TD([[makeQuery(id+"F2.imprint","IMPRINT",EDGE,{"derivedFrom":subQ5}),-1.0]])]});}
            var Q79;
            {var subQ0=sQuery(id+"F2.wireOp",EDGE,"E23.1.6");var subQ1=sQuery(id+"F2.wireOp",EDGE,"E16");var subQ2=makeQuery(id+"F2.imprint","INTERSECT",VERTEX,{"derivedFrom":[subQ1,subQ0]});Q79=makeQuery(id+"F2.imprint","IMPRINT",FACE,{"disambiguationData":[TD([[makeQuery(id+"F2.imprint","IMPRINT",EDGE,{"disambiguationData":[TD([[subQ2,-1.0]])],"derivedFrom":subQ1}),-1.0]])]});}
            var Q80;
            {var subQ0=sQuery(id+"F2.wireOp",EDGE,"E10");var subQ1=sQuery(id+"F2.wireOp",EDGE,"E9");var subQ2=makeQuery(id+"F2.imprint","INTERSECT",VERTEX,{"derivedFrom":[subQ1,subQ0]});Q80=makeQuery(id+"F2.imprint","IMPRINT",FACE,{"disambiguationData":[TD([[makeQuery(id+"F2.imprint","IMPRINT",EDGE,{"disambiguationData":[TD([[subQ2,-1.0]])],"derivedFrom":subQ1}),1.0]])]});}
            var Q81;
            {var subQ0=sQuery(id+"F2.wireOp",EDGE,"E24.20.4.0");var subQ1=sQuery(id+"F2.wireOp",EDGE,"E16");var subQ2=makeQuery(id+"F2.imprint","INTERSECT",VERTEX,{"derivedFrom":[subQ1,subQ0]});Q81=makeQuery(id+"F2.imprint","IMPRINT",FACE,{"disambiguationData":[TD([[makeQuery(id+"F2.imprint","IMPRINT",EDGE,{"disambiguationData":[TD([[subQ2,-1.0]])],"derivedFrom":subQ1}),-1.0]])]});}
            var Q82;
            {var subQ0=sQuery(id+"F2.wireOp",EDGE,"E24.20.3.0");var subQ1=sQuery(id+"F2.wireOp",EDGE,"E16");var subQ2=makeQuery(id+"F2.imprint","INTERSECT",VERTEX,{"derivedFrom":[subQ1,subQ0]});Q82=makeQuery(id+"F2.imprint","IMPRINT",FACE,{"disambiguationData":[TD([[makeQuery(id+"F2.imprint","IMPRINT",EDGE,{"disambiguationData":[TD([[subQ2,-1.0]])],"derivedFrom":subQ1}),-1.0]])]});}
            var Q83;
            {var subQ0=sQuery(id+"F2.wireOp",EDGE,"E23.2.6");var subQ1=sQuery(id+"F2.wireOp",EDGE,"E16");var subQ2=makeQuery(id+"F2.imprint","INTERSECT",VERTEX,{"derivedFrom":[subQ1,subQ0]});Q83=makeQuery(id+"F2.imprint","IMPRINT",FACE,{"disambiguationData":[TD([[makeQuery(id+"F2.imprint","IMPRINT",EDGE,{"disambiguationData":[TD([[subQ2,-1.0]])],"derivedFrom":subQ1}),-1.0]])]});}
            extrude(context, id + "F3", {"entities" : qUnion([Q0, Q1, Q2, Q3, Q4, Q5, Q6, Q7, Q8, Q9, Q10, Q11, Q12, Q13, Q14, Q15, Q16, Q17, Q18, Q19, Q20, Q21, Q22, Q23, Q24, Q25, Q26, Q27, Q28, Q29, Q30, Q31, Q32, Q33, Q34, Q35, Q36, Q37, Q38, Q39, Q40, Q41, Q42, Q43, Q44, Q45, Q46, Q47, Q48, Q49, Q50, Q51, Q52, Q53, Q54, Q55, Q56, Q57, Q58, Q59, Q60, Q61, Q62, Q63, Q64, Q65, Q66, Q67, Q68, Q69, Q70, Q71, Q72, Q73, Q74, Q75, Q76, Q77, Q78, Q79, Q80, Q81, Q82, Q83]), "operationType" : NewBodyOperationType.ADD, "depth" : 0.5 * mm, "offsetDistance" : 25 * mm});
        }
        {
            var Q0;
            {var subQ9=sQuery(id+"F2.wireOp",EDGE,"E23.1.7");Q0=makeQuery(id+"F2.imprint","IMPRINT",FACE,{"disambiguationData":[TD([[makeQuery(id+"F2.imprint","IMPRINT",EDGE,{"derivedFrom":subQ9}),1.0]])]});}
            var Q1;
            {var subQ0=sQuery(id+"F2.wireOp",EDGE,"E11");Q1=makeQuery(id+"F2.imprint","IMPRINT",FACE,{"disambiguationData":[TD([[makeQuery(id+"F2.imprint","IMPRINT",EDGE,{"derivedFrom":subQ0}),1.0]])]});}
            var Q2;
            {var subQ7=sQuery(id+"F2.wireOp",EDGE,"E24.23.4.0");Q2=makeQuery(id+"F2.imprint","IMPRINT",FACE,{"disambiguationData":[TD([[makeQuery(id+"F2.imprint","IMPRINT",EDGE,{"derivedFrom":subQ7}),1.0]])]});}
            var Q3;
            {var subQ5=sQuery(id+"F2.wireOp",EDGE,"E24.23.3.0");Q3=makeQuery(id+"F2.imprint","IMPRINT",FACE,{"disambiguationData":[TD([[makeQuery(id+"F2.imprint","IMPRINT",EDGE,{"derivedFrom":subQ5}),1.0]])]});}
            var Q4;
            {var subQ5=sQuery(id+"F2.wireOp",EDGE,"E23.2.7");Q4=makeQuery(id+"F2.imprint","IMPRINT",FACE,{"disambiguationData":[TD([[makeQuery(id+"F2.imprint","IMPRINT",EDGE,{"derivedFrom":subQ5}),1.0]])]});}
            extrude(context, id + "F4", {"entities" : qUnion([Q0, Q1, Q2, Q3, Q4]), "operationType" : NewBodyOperationType.ADD, "depth" : 0.3 * mm, "offsetDistance" : 25 * mm});
        }
    });
